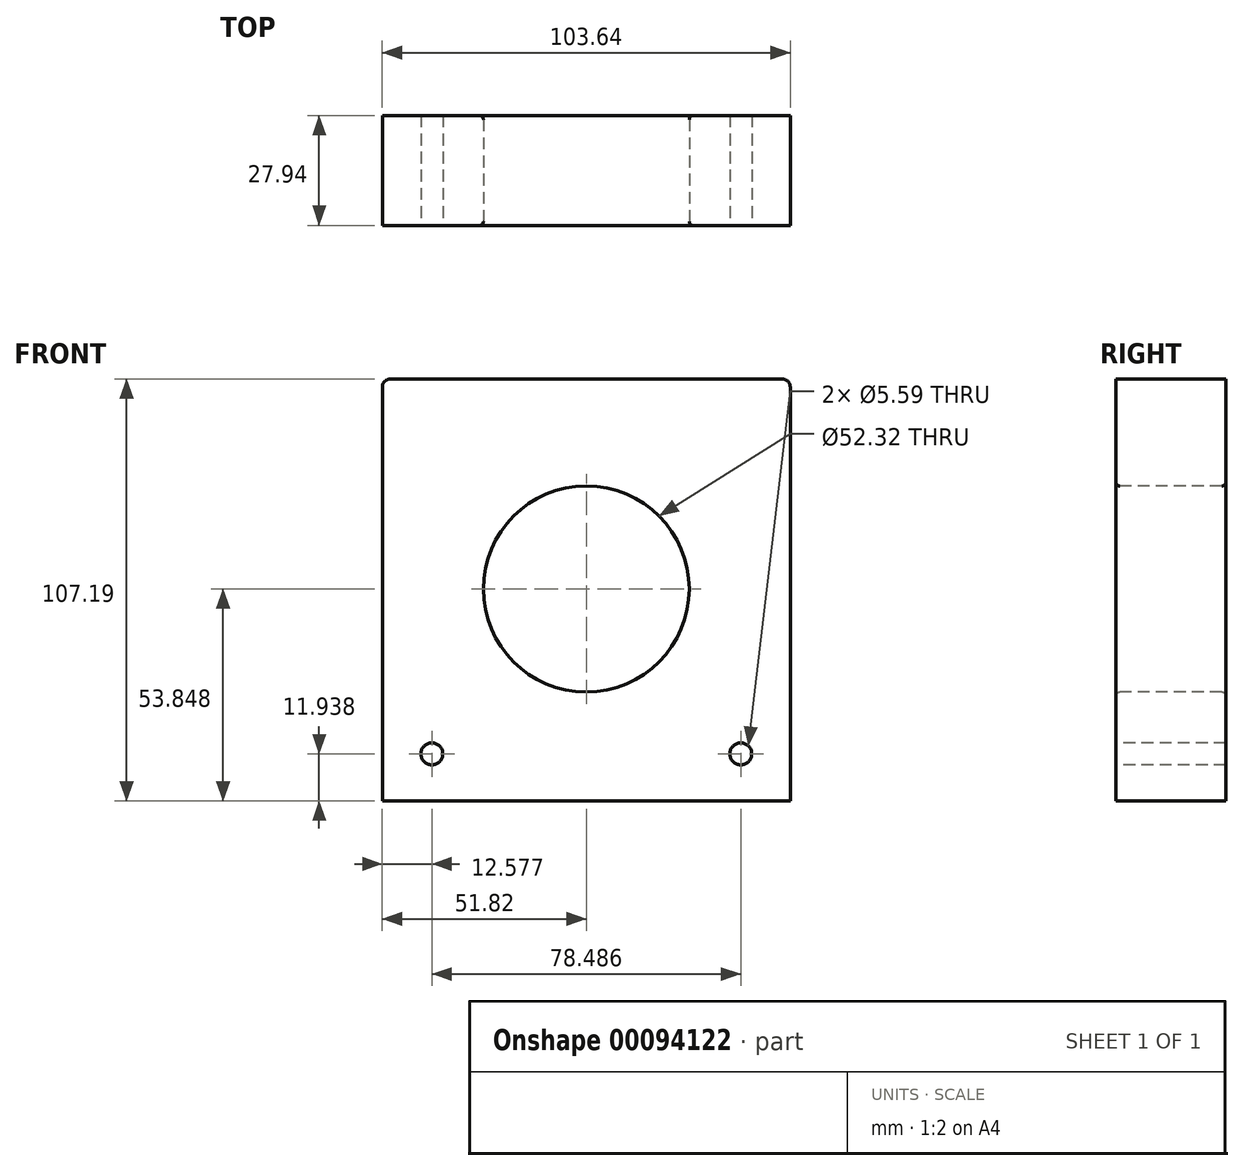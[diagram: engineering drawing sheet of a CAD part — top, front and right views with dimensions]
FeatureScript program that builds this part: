
annotation { "Feature Type Name" : "Feature", "Feature Type Description" : "" }
export const myFeature = defineFeature(function(context is Context, id is Id, definition is map)
    precondition{}
    {
        {
            var Q0;
            Q0=qCreatedBy(makeId("Top.planeOp"),FACE);
            var sketch = newSketch(context, id + "F0", { "sketchPlane" : qUnion([Q0])});
            skLineSegment(sketch, "E0.bottom", {"start": v(51.82, -13.97) * mm, "end": v(-51.82, -13.97) * mm});
            skLineSegment(sketch, "E0.top", {"start": v(51.82, 13.97) * mm, "end": v(-51.82, 13.97) * mm});
            skLineSegment(sketch, "E0.left", {"start": v(51.82, -13.97) * mm, "end": v(51.82, 13.97) * mm});
            skLineSegment(sketch, "E0.right", {"start": v(-51.82, -13.97) * mm, "end": v(-51.82, 13.97) * mm});
            skPoint(sketch, "E0.middle", {"position": v(0, 0) * mm});
            skSolve(sketch);
        }
        {
            var Q0;
            Q0=makeQuery(id+"F0.imprint","IMPRINT",FACE,{"disambiguationData":[TD([[makeQuery(id+"F0.imprint","IMPRINT",EDGE,{"derivedFrom":sQuery(id+"F0.wireOp",EDGE,"E0.bottom")}),-1.0]])]});
            extrude(context, id + "F1", {"entities" : qUnion([Q0]), "depth" : 107.19 * mm});
        }
        {
            var Q0;
            Q0=makeQuery(id+"F1.opExtrude","SWEPT_FACE",FACE,{"disambiguationData":[OSD([sQuery(id+"F0.wireOp",EDGE,"E0.bottom")])]});
            var sketch = newSketch(context, id + "F2", { "sketchPlane" : qUnion([Q0])});
            skCircle(sketch, "E1", {"center": v(0, 53.85) * mm, "radius": 26.16 * mm});
            skSolve(sketch);
        }
        {
            var Q0;
            Q0=makeQuery(id+"F2.imprint","IMPRINT",FACE,{"disambiguationData":[TD([[makeQuery(id+"F2.imprint","IMPRINT",EDGE,{"derivedFrom":sQuery(id+"F2.wireOp",EDGE,"E1")}),1.0]])]});
            extrude(context, id + "F3", {"entities" : qUnion([Q0]), "operationType" : NewBodyOperationType.REMOVE, "endBound" : BoundingType.THROUGH_ALL, "oppositeDirection" : true, "depth" : 25 * mm});
        }
        {
            var Q0;
            Q0=makeQuery(id+"F1.opExtrude","SWEPT_FACE",FACE,{"disambiguationData":[OSD([sQuery(id+"F0.wireOp",EDGE,"E0.bottom")])]});
            var sketch = newSketch(context, id + "F4", { "sketchPlane" : qUnion([Q0])});
            skCircle(sketch, "E2", {"center": v(-39.24, 11.94) * mm, "radius": 2.8 * mm});
            skCircle(sketch, "E3", {"center": v(39.24, 11.94) * mm, "radius": 2.8 * mm});
            skSolve(sketch);
        }
        {
            var Q0;
            Q0=makeQuery(id+"F4.imprint","IMPRINT",FACE,{"disambiguationData":[TD([[makeQuery(id+"F4.imprint","IMPRINT",EDGE,{"derivedFrom":sQuery(id+"F4.wireOp",EDGE,"E2")}),1.0]])]});
            var Q1;
            Q1=makeQuery(id+"F4.imprint","IMPRINT",FACE,{"disambiguationData":[TD([[makeQuery(id+"F4.imprint","IMPRINT",EDGE,{"derivedFrom":sQuery(id+"F4.wireOp",EDGE,"E3")}),1.0]])]});
            extrude(context, id + "F5", {"entities" : qUnion([Q0, Q1]), "operationType" : NewBodyOperationType.REMOVE, "endBound" : BoundingType.THROUGH_ALL, "oppositeDirection" : true, "depth" : 25 * mm});
        }
        {
            var Q0;
            Q0=makeQuery(id+"F3.boolean.opBoolean","COPY",FACE,{"derivedFrom":makeQuery(id+"F3.opExtrude","SWEPT_FACE",FACE,{"disambiguationData":[OSD([sQuery(id+"F2.wireOp",EDGE,"E1")])]})});
            fillet(context, id + "F6", {"entities" : qUnion([Q0]), "radius" : 1 * mm, "tangentPropagation" : true, "allowEdgeOverflow" : false});
        }
        {
            var Q0;
            Q0=makeQuery(id+"F1.opExtrude","CAP_EDGE",EDGE,{"disambiguationData":[OSD([sQuery(id+"F0.wireOp",EDGE,"E0.left")])],"isStart":false});
            var Q1;
            Q1=makeQuery(id+"F1.opExtrude","CAP_EDGE",EDGE,{"disambiguationData":[OSD([sQuery(id+"F0.wireOp",EDGE,"E0.right")])],"isStart":false});
            fillet(context, id + "F7", {"entities" : qUnion([Q0, Q1]), "radius" : 2 * mm, "tangentPropagation" : true, "allowEdgeOverflow" : false});
        }
    });
